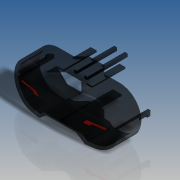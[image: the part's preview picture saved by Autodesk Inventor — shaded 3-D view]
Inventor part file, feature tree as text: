
AUTODESK INVENTOR PART (.ipt)
format: ipt  version: 2016 SP2 (Build 200236200, 236)  size: 815,104 bytes
history: native  units: in
note: dims shown in document units (in); Inventor stores cm internally (conversion verified against a paired STEP export)
features: extrude x18, sketch x8, fillet x2, plane x1, mirror x1, other x1
ambient origin geometry x8: Origin, YZ Plane, XZ Plane, XY Plane, X Axis, Y Axis, Z Axis, Center Point
bodies: Solid1 (feature_tree)
feature tree (31):
  extrude  "Extrusion1"  Depth=0.6299in
  sketch  "Sketch3"  dims[d2=0.4961in d3=2.1732in]
  extrude  "Extrusion2"  Depth=2.1732in
  extrude  "Extrusion3"  Depth=0.315in
  sketch  "Sketch4"  dims[d4=0.1575in d5=0.315in]
  extrude  "Extrusion4"  Depth=0.6299in TaperAngle=0.0deg
  extrude  "Extrusion5"  Depth=0.0547in
  fillet  "Fillet1"  Radius=0.7559in
  sketch  "Sketch5"  dims[d6=0.6299in d7=0.9134in d8=0.0in]
  plane  "Work Plane1"
  extrude  "Extrusion10"  Depth=0.315in
  extrude  "Extrusion11"  Depth=0.6597in
  extrude  "Extrusion12"  Depth=0.0039in
  sketch  "Sketch8"  dims[d12=0.2693in d13=0.315in]
  extrude  "Extrusion13"  Depth=0.0039in
  extrude  "Extrusion14"  Depth=0.0039in
  extrude  "Extrusion15"  Depth=0.0315in
  extrude  "Extrusion16"  Depth=0.3937in TaperAngle=0.0deg
  extrude  "Extrusion17"  TaperAngle=0.0deg  [1 undecoded]
  extrude  "Extrusion18"  Depth=0.315in
  extrude  "Extrusion19"  Depth=0.315in
  extrude  "Extrusion20"  Depth=0.0039in
  extrude  "Extrusion21"  Depth=0.6299in
  extrude  "Extrusion22"  Depth=0.3937in TaperAngle=0.0deg
  mirror  "Mirror2"
  fillet  "Fillet2"  Radius=0.3937in
  sketch  "Sketch2"  dims[d0=2.4409in d1=0.6299in]
  sketch  "Sketch7"  dims[d9=0.0547in d10=0.0507in d11=0.7559in]
  sketch  "Sketch9"  dims[d14=0.9449in d18=0.6597in]
  sketch  "Sketch10"  dims[d19=0.2189in d20=0.6614in d21=0.0507in d22=0.0507in d23=0.0315in d24=0.3937in d25=0.0in d26=0.0in d27=0.0in d29=0.315in d30=0.315in d31=0.1575in d32=0.6299in d33=0.3937in d34=0.0in d35=0.3937in d36=0.0in d37=0.0457in d39=0.0457in d40=0.0236in d41=0.0472in d42=0.063in d51=0.3937in d52=0.0in d53=0.3937in d54=0.0in d55=0.3937in d56=0.0in d57=0.3937in d58=0.0in d59=0.3937in d60=0.0in d61=0.3937in d62=0.0in d63=0.2992in d64=0.0in d65=0.126in d66=0.0315in d67=0.063in d68=0.1575in d69=0.4724in d70=0.189in d71=0.0315in d72=0.6614in d73=0.1811in d74=0.0in d75=0.0in d76=0.3937in d77=0.2992in d78=0.0in d79=0.0in d80=0.5827in d81=0.0in d82=0.5827in d83=0.0in d84=0.3178in d85=0.0677in d86=0.0457in d87=0.063in d88=0.0441in d89=0.0504in d90=0.0598in d91=0.252in d92=0.0315in d93=0.063in d94=0.0in d95=0.1685in d96=0.1657in d97=0.0378in d98=0.0787in d99=0.2693in d100=0.9118in d101=0.0961in d102=0.0157in d103=0.0094in d106=0.0in d107=0.0in d108=0.0039in]
  other  "Eyes"
note: 1 required parameter value undecoded (feature->parameter linkage not recoverable at this tier; creation-order binding heuristic only, values carry confidence <= 0.55)
